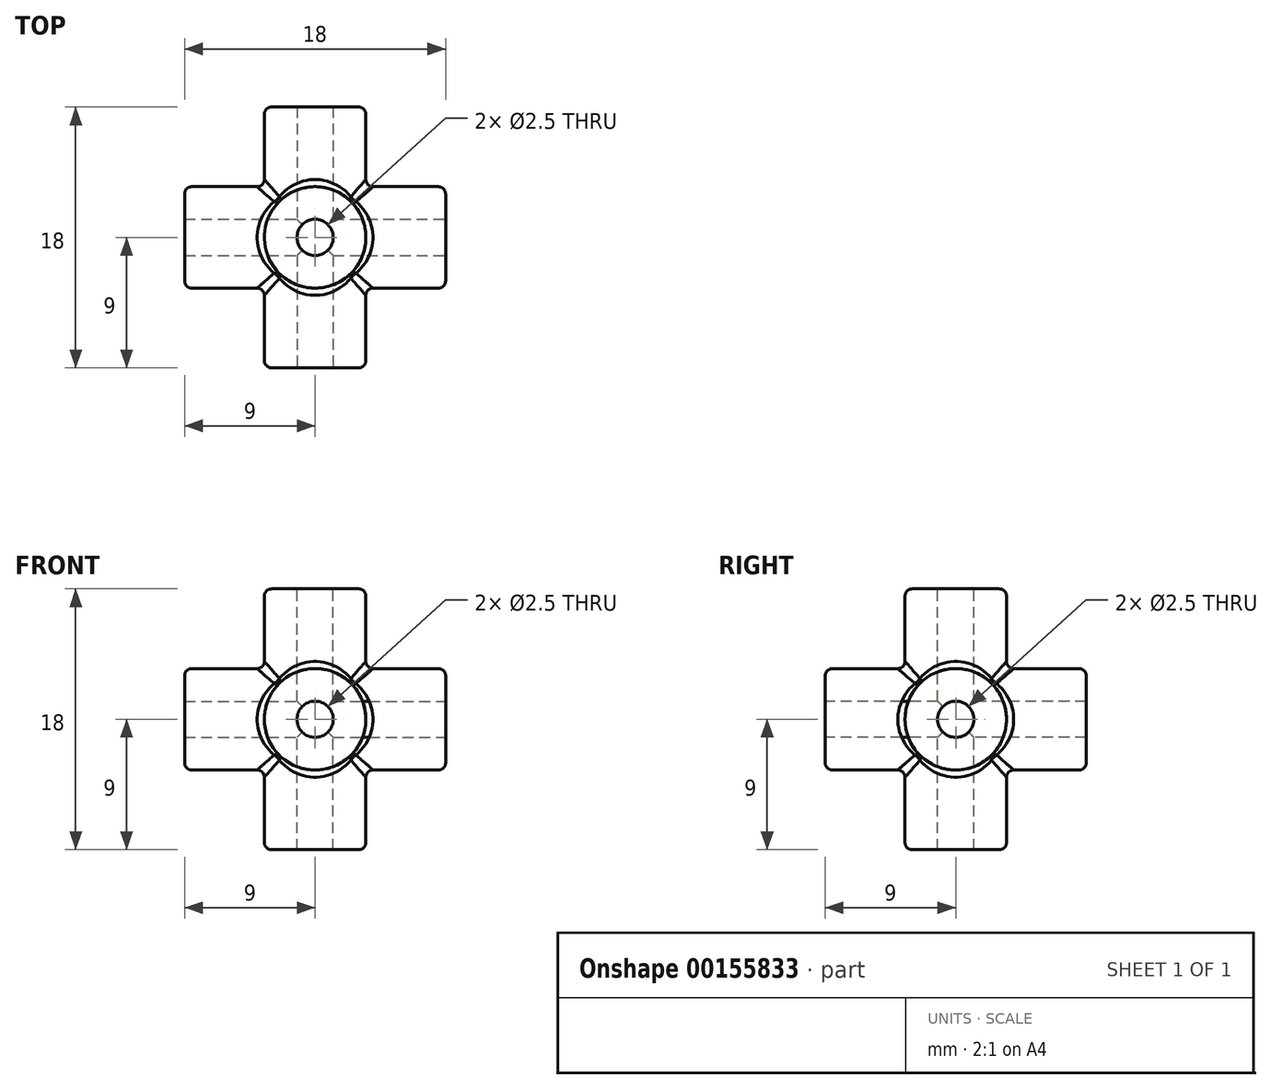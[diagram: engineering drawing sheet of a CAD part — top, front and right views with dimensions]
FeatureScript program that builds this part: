
annotation { "Feature Type Name" : "Feature", "Feature Type Description" : "" }
export const myFeature = defineFeature(function(context is Context, id is Id, definition is map)
    precondition{}
    {
        {
            var Q0;
            Q0=qCreatedBy(makeId("Front.planeOp"),FACE);
            var sketch = newSketch(context, id + "F0", { "sketchPlane" : qUnion([Q0])});
            skCircle(sketch, "E0", {"center": v(0, 0) * mm, "radius": 3.5 * mm});
            skSolve(sketch);
        }
        {
            var Q0;
            Q0=makeQuery(id+"F0.imprint","IMPRINT",FACE,{"disambiguationData":[TD([[makeQuery(id+"F0.imprint","IMPRINT",EDGE,{"derivedFrom":sQuery(id+"F0.wireOp",EDGE,"E0")}),1.0]])]});
            extrude(context, id + "F1", {"entities" : qUnion([Q0]), "endBound" : BoundingType.SYMMETRIC, "depth" : 18 * mm});
        }
        {
            var Q0;
            Q0=qCreatedBy(makeId("Right.planeOp"),FACE);
            var sketch = newSketch(context, id + "F2", { "sketchPlane" : qUnion([Q0])});
            skCircle(sketch, "E1", {"center": v(0, 0) * mm, "radius": 3.5 * mm});
            skSolve(sketch);
        }
        {
            var Q0;
            Q0 = qSketchRegion(id + "F2", true);
            extrude(context, id + "F3", {"entities" : qUnion([Q0]), "operationType" : NewBodyOperationType.ADD, "endBound" : BoundingType.SYMMETRIC, "depth" : 18 * mm});
        }
        {
            var Q0;
            Q0=qCreatedBy(makeId("Top.planeOp"),FACE);
            var sketch = newSketch(context, id + "F4", { "sketchPlane" : qUnion([Q0])});
            skCircle(sketch, "E2", {"center": v(0, 0) * mm, "radius": 3.5 * mm});
            skSolve(sketch);
        }
        {
            var Q0;
            Q0 = qSketchRegion(id + "F4", true);
            extrude(context, id + "F5", {"entities" : qUnion([Q0]), "operationType" : NewBodyOperationType.ADD, "endBound" : BoundingType.SYMMETRIC, "depth" : 18 * mm});
        }
        {
            var Q0;
            Q0=makeQuery(id+"F5.opExtrude","CAP_FACE",FACE,{"disambiguationData":[OSD([sQuery(id+"F4.wireOp",EDGE,"E2")])],"isStart":false});
            var sketch = newSketch(context, id + "F6", { "sketchPlane" : qUnion([Q0])});
            skCircle(sketch, "E3", {"center": v(0, 0) * mm, "radius": 1.25 * mm});
            skSolve(sketch);
        }
        {
            var Q0;
            Q0 = qSketchRegion(id + "F6", true);
            extrude(context, id + "F7", {"entities" : qUnion([Q0]), "operationType" : NewBodyOperationType.REMOVE, "endBound" : BoundingType.THROUGH_ALL, "oppositeDirection" : true, "depth" : 25 * mm});
        }
        {
            var Q0;
            Q0=makeQuery(id+"F3.opExtrude","CAP_FACE",FACE,{"disambiguationData":[OSD([sQuery(id+"F2.wireOp",EDGE,"E1")])],"isStart":false});
            var sketch = newSketch(context, id + "F8", { "sketchPlane" : qUnion([Q0])});
            skCircle(sketch, "E4", {"center": v(0, 0) * mm, "radius": 1.25 * mm});
            skSolve(sketch);
        }
        {
            var Q0;
            Q0 = qSketchRegion(id + "F8", true);
            extrude(context, id + "F9", {"entities" : qUnion([Q0]), "operationType" : NewBodyOperationType.REMOVE, "endBound" : BoundingType.THROUGH_ALL, "oppositeDirection" : true, "depth" : 25 * mm});
        }
        {
            var Q0;
            Q0=makeQuery(id+"F1.opExtrude","CAP_FACE",FACE,{"disambiguationData":[OSD([sQuery(id+"F0.wireOp",EDGE,"E0")])],"isStart":false});
            var sketch = newSketch(context, id + "F10", { "sketchPlane" : qUnion([Q0])});
            skCircle(sketch, "E5", {"center": v(0, 0) * mm, "radius": 1.25 * mm});
            skSolve(sketch);
        }
        {
            var Q0;
            Q0 = qSketchRegion(id + "F10", true);
            extrude(context, id + "F11", {"entities" : qUnion([Q0]), "operationType" : NewBodyOperationType.REMOVE, "endBound" : BoundingType.THROUGH_ALL, "oppositeDirection" : true, "depth" : 25 * mm});
        }
        {
            var Q0;
            Q0=makeQuery(id+"F1.opExtrude","CAP_EDGE",EDGE,{"disambiguationData":[OSD([sQuery(id+"F0.wireOp",EDGE,"E0")])],"isStart":false});
            var Q1;
            Q1=makeQuery(id+"F3.opExtrude","CAP_EDGE",EDGE,{"disambiguationData":[OSD([sQuery(id+"F2.wireOp",EDGE,"E1")])],"isStart":true});
            var Q2;
            Q2=makeQuery(id+"F5.opExtrude","CAP_EDGE",EDGE,{"disambiguationData":[OSD([sQuery(id+"F4.wireOp",EDGE,"E2")])],"isStart":true});
            var Q3;
            Q3=makeQuery(id+"F1.opExtrude","CAP_EDGE",EDGE,{"disambiguationData":[OSD([sQuery(id+"F0.wireOp",EDGE,"E0")])],"isStart":true});
            var Q4;
            Q4=makeQuery(id+"F5.opExtrude","CAP_EDGE",EDGE,{"disambiguationData":[OSD([sQuery(id+"F4.wireOp",EDGE,"E2")])],"isStart":false});
            var Q5;
            Q5=makeQuery(id+"F3.opExtrude","CAP_EDGE",EDGE,{"disambiguationData":[OSD([sQuery(id+"F2.wireOp",EDGE,"E1")])],"isStart":false});
            var Q6;
            {var subQ0=sQuery(id+"F0.wireOp",EDGE,"E0");var subQ1=makeQuery(id+"F1.opExtrude","SWEPT_FACE",FACE,{"disambiguationData":[OSD([subQ0])]});Q6=makeQuery(id+"F5.boolean.opBoolean","INTERSECT",EDGE,{"disambiguationData":[OD(1.0)],"derivedFrom":[makeQuery(id+"F3.boolean.opBoolean","SPLIT",FACE,{"disambiguationData":[TD([makeQuery(id+"F1.opExtrude","CAP_FACE",FACE,{"disambiguationData":[OSD([subQ0])],"isStart":false})])],"derivedFrom":subQ1}),makeQuery(id+"F5.opExtrude","SWEPT_FACE",FACE,{"disambiguationData":[OSD([sQuery(id+"F4.wireOp",EDGE,"E2")])]})]});}
            var Q7;
            {var subQ0=sQuery(id+"F2.wireOp",EDGE,"E1");var subQ1=makeQuery(id+"F3.opExtrude","SWEPT_FACE",FACE,{"disambiguationData":[OSD([subQ0])]});Q7=makeQuery(id+"F5.boolean.opBoolean","INTERSECT",EDGE,{"disambiguationData":[OD(1.0)],"derivedFrom":[makeQuery(id+"F3.boolean.opBoolean","SPLIT",FACE,{"disambiguationData":[TD([makeQuery(id+"F3.opExtrude","CAP_FACE",FACE,{"disambiguationData":[OSD([subQ0])],"isStart":false})])],"derivedFrom":subQ1}),makeQuery(id+"F5.opExtrude","SWEPT_FACE",FACE,{"disambiguationData":[OSD([sQuery(id+"F4.wireOp",EDGE,"E2")])]})]});}
            var Q8;
            Q8=makeQuery(id+"F3.boolean.opBoolean","INTERSECT",EDGE,{"disambiguationData":[OD(3.0)],"derivedFrom":[makeQuery(id+"F1.opExtrude","SWEPT_FACE",FACE,{"disambiguationData":[OSD([sQuery(id+"F0.wireOp",EDGE,"E0")])]}),makeQuery(id+"F3.opExtrude","SWEPT_FACE",FACE,{"disambiguationData":[OSD([sQuery(id+"F2.wireOp",EDGE,"E1")])]})]});
            var Q9;
            {var subQ0=sQuery(id+"F0.wireOp",EDGE,"E0");var subQ1=makeQuery(id+"F1.opExtrude","SWEPT_FACE",FACE,{"disambiguationData":[OSD([subQ0])]});Q9=makeQuery(id+"F5.boolean.opBoolean","INTERSECT",EDGE,{"disambiguationData":[OD(1.0)],"derivedFrom":[makeQuery(id+"F3.boolean.opBoolean","SPLIT",FACE,{"disambiguationData":[TD([makeQuery(id+"F1.opExtrude","CAP_FACE",FACE,{"disambiguationData":[OSD([subQ0])],"isStart":true})])],"derivedFrom":subQ1}),makeQuery(id+"F5.opExtrude","SWEPT_FACE",FACE,{"disambiguationData":[OSD([sQuery(id+"F4.wireOp",EDGE,"E2")])]})]});}
            var Q10;
            Q10=makeQuery(id+"F3.boolean.opBoolean","INTERSECT",EDGE,{"disambiguationData":[OD(1.0)],"derivedFrom":[makeQuery(id+"F1.opExtrude","SWEPT_FACE",FACE,{"disambiguationData":[OSD([sQuery(id+"F0.wireOp",EDGE,"E0")])]}),makeQuery(id+"F3.opExtrude","SWEPT_FACE",FACE,{"disambiguationData":[OSD([sQuery(id+"F2.wireOp",EDGE,"E1")])]})]});
            var Q11;
            {var subQ0=sQuery(id+"F0.wireOp",EDGE,"E0");var subQ1=makeQuery(id+"F1.opExtrude","SWEPT_FACE",FACE,{"disambiguationData":[OSD([subQ0])]});Q11=makeQuery(id+"F5.boolean.opBoolean","INTERSECT",EDGE,{"disambiguationData":[OD(0.0)],"derivedFrom":[makeQuery(id+"F3.boolean.opBoolean","SPLIT",FACE,{"disambiguationData":[TD([makeQuery(id+"F1.opExtrude","CAP_FACE",FACE,{"disambiguationData":[OSD([subQ0])],"isStart":true})])],"derivedFrom":subQ1}),makeQuery(id+"F5.opExtrude","SWEPT_FACE",FACE,{"disambiguationData":[OSD([sQuery(id+"F4.wireOp",EDGE,"E2")])]})]});}
            var Q12;
            Q12=makeQuery(id+"F3.boolean.opBoolean","INTERSECT",EDGE,{"disambiguationData":[OD(0.0)],"derivedFrom":[makeQuery(id+"F1.opExtrude","SWEPT_FACE",FACE,{"disambiguationData":[OSD([sQuery(id+"F0.wireOp",EDGE,"E0")])]}),makeQuery(id+"F3.opExtrude","SWEPT_FACE",FACE,{"disambiguationData":[OSD([sQuery(id+"F2.wireOp",EDGE,"E1")])]})]});
            var Q13;
            {var subQ0=sQuery(id+"F2.wireOp",EDGE,"E1");var subQ1=makeQuery(id+"F3.opExtrude","SWEPT_FACE",FACE,{"disambiguationData":[OSD([subQ0])]});Q13=makeQuery(id+"F5.boolean.opBoolean","INTERSECT",EDGE,{"disambiguationData":[OD(0.0)],"derivedFrom":[makeQuery(id+"F3.boolean.opBoolean","SPLIT",FACE,{"disambiguationData":[TD([makeQuery(id+"F3.opExtrude","CAP_FACE",FACE,{"disambiguationData":[OSD([subQ0])],"isStart":true})])],"derivedFrom":subQ1}),makeQuery(id+"F5.opExtrude","SWEPT_FACE",FACE,{"disambiguationData":[OSD([sQuery(id+"F4.wireOp",EDGE,"E2")])]})]});}
            var Q14;
            {var subQ0=sQuery(id+"F2.wireOp",EDGE,"E1");var subQ1=makeQuery(id+"F3.opExtrude","SWEPT_FACE",FACE,{"disambiguationData":[OSD([subQ0])]});Q14=makeQuery(id+"F5.boolean.opBoolean","INTERSECT",EDGE,{"disambiguationData":[OD(0.0)],"derivedFrom":[makeQuery(id+"F3.boolean.opBoolean","SPLIT",FACE,{"disambiguationData":[TD([makeQuery(id+"F3.opExtrude","CAP_FACE",FACE,{"disambiguationData":[OSD([subQ0])],"isStart":false})])],"derivedFrom":subQ1}),makeQuery(id+"F5.opExtrude","SWEPT_FACE",FACE,{"disambiguationData":[OSD([sQuery(id+"F4.wireOp",EDGE,"E2")])]})]});}
            var Q15;
            {var subQ0=sQuery(id+"F0.wireOp",EDGE,"E0");var subQ1=makeQuery(id+"F1.opExtrude","SWEPT_FACE",FACE,{"disambiguationData":[OSD([subQ0])]});Q15=makeQuery(id+"F5.boolean.opBoolean","INTERSECT",EDGE,{"disambiguationData":[OD(0.0)],"derivedFrom":[makeQuery(id+"F3.boolean.opBoolean","SPLIT",FACE,{"disambiguationData":[TD([makeQuery(id+"F1.opExtrude","CAP_FACE",FACE,{"disambiguationData":[OSD([subQ0])],"isStart":false})])],"derivedFrom":subQ1}),makeQuery(id+"F5.opExtrude","SWEPT_FACE",FACE,{"disambiguationData":[OSD([sQuery(id+"F4.wireOp",EDGE,"E2")])]})]});}
            var Q16;
            Q16=makeQuery(id+"F3.boolean.opBoolean","INTERSECT",EDGE,{"disambiguationData":[OD(2.0)],"derivedFrom":[makeQuery(id+"F1.opExtrude","SWEPT_FACE",FACE,{"disambiguationData":[OSD([sQuery(id+"F0.wireOp",EDGE,"E0")])]}),makeQuery(id+"F3.opExtrude","SWEPT_FACE",FACE,{"disambiguationData":[OSD([sQuery(id+"F2.wireOp",EDGE,"E1")])]})]});
            var Q17;
            {var subQ0=sQuery(id+"F2.wireOp",EDGE,"E1");var subQ1=makeQuery(id+"F3.opExtrude","SWEPT_FACE",FACE,{"disambiguationData":[OSD([subQ0])]});Q17=makeQuery(id+"F5.boolean.opBoolean","INTERSECT",EDGE,{"disambiguationData":[OD(1.0)],"derivedFrom":[makeQuery(id+"F3.boolean.opBoolean","SPLIT",FACE,{"disambiguationData":[TD([makeQuery(id+"F3.opExtrude","CAP_FACE",FACE,{"disambiguationData":[OSD([subQ0])],"isStart":true})])],"derivedFrom":subQ1}),makeQuery(id+"F5.opExtrude","SWEPT_FACE",FACE,{"disambiguationData":[OSD([sQuery(id+"F4.wireOp",EDGE,"E2")])]})]});}
            fillet(context, id + "F12", {"entities" : qUnion([Q0, Q1, Q2, Q3, Q4, Q5, Q6, Q7, Q8, Q9, Q10, Q11, Q12, Q13, Q14, Q15, Q16, Q17]), "radius" : .5 * mm, "tangentPropagation" : true, "allowEdgeOverflow" : false});
        }
    });
